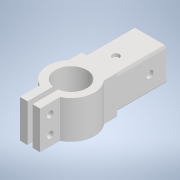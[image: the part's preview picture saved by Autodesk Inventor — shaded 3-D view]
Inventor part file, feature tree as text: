
AUTODESK INVENTOR PART (.ipt)
format: ipt  version: 2020 (Build 240168000, 168)  size: 293,888 bytes
history: native  units: mm
features: sketch x14, extrude x11, hole x3
ambient origin geometry x8: Origin, YZ Plane, XZ Plane, XY Plane, X Axis, Y Axis, Z Axis, Center Point
bodies: Solido1 (feature_tree)
feature tree (28):
  extrude  "Estrusione1"  Depth=18.0mm
  extrude  "Estrusione2"  Depth=40.0mm TaperAngle=0.0deg
  extrude  "Estrusione3"  Depth=30.0mm
  extrude  "Estrusione4"  Depth=37.0mm
  extrude  "Estrusione5"  Depth=50.0mm TaperAngle=0.0deg
  extrude  "Estrusione6"  Depth=22.5mm
  extrude  "Estrusione7"  TaperAngle=90.0deg  [1 undecoded]
  extrude  "Estrusione8"  Depth=25.0mm
  extrude  "Estrusione9"  Depth=30.0mm TaperAngle=0.0deg
  hole  "Foro1"  [1 undecoded]
  extrude  "Estrusione10"  Depth=2.0mm
  extrude  "Estrusione11"  TaperAngle=0.0deg  [1 undecoded]
  hole  "Foro4"  [1 undecoded]
  hole  "Foro5"  [1 undecoded]
  sketch  "Schizzo1"
  sketch  "Schizzo2"
  sketch  "Schizzo3"
  sketch  "Schizzo4"
  sketch  "Schizzo5"
  sketch  "Schizzo6"
  sketch  "Schizzo7"
  sketch  "Schizzo8"
  sketch  "Schizzo10"
  sketch  "Schizzo11"
  sketch  "Schizzo14"
  sketch  "Schizzo15"
  sketch  "Schizzo16"
  sketch  "Schizzo17"
note: 5 required parameter values undecoded (feature->parameter linkage not recoverable at this tier; creation-order binding heuristic only, values carry confidence <= 0.55)
